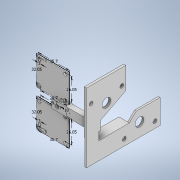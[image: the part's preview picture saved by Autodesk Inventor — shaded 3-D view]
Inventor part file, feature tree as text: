
AUTODESK INVENTOR PART (.ipt)
format: ipt  version: 2020.2 (Build 242310000, 310)  size: 299,008 bytes
history: native  units: mm
features: sketch x12, extrude x9, hole x4, projected_geometry x2
ambient origin geometry x8: Origin, YZ Plane, XZ Plane, XY Plane, X Axis, Y Axis, Z Axis, Center Point
bodies: Body1 (feature_tree)
feature tree (27):
  extrude  "Extrusion7"  Depth=6.08mm
  hole  "Hole4"  [1 undecoded]
  sketch  "Sketch16"  dims[d70=12.16mm d71=10.0mm]
  extrude  "Extrusion8"  Depth=10.0mm
  hole  "Hole5"  [1 undecoded]
  extrude  "Extrusion9"  Depth=32.05mm
  extrude  "Extrusion10"  Depth=32.05mm
  extrude  "Extrusion11"  Depth=3.0mm
  extrude  "Extrusion12"  Depth=26.05mm
  hole  "Hole6"  [1 undecoded]
  hole  "Hole7"  [1 undecoded]
  extrude  "Extrusion13"  Depth=4.0mm TaperAngle=0.0deg
  extrude  "Extrusion14"  Depth=35.0mm TaperAngle=0.0deg
  extrude  "Extrusion15"  Depth=10.0mm
  sketch  "Sketch14"  dims[d66=6.08mm d67=6.08mm]
  sketch  "Sketch15"  dims[d68=5.0mm d69=90.0deg]
  sketch  "Sketch17"  dims[d72=2.0mm d73=0.0mm]
  projected_geometry  "Projected Loop2"
  sketch  "Sketch18"  dims[d74=4.5mm d75=6.0mm d76=9.4mm d77=2.0mm d78=90.0deg d79=8.0mm d80=20.594885mm d81=10.0mm]
  projected_geometry  "Projected Loop3"
  sketch  "Sketch19"  dims[d82=35.7mm d83=32.05mm]
  sketch  "Sketch20"  dims[d84=35.7mm d85=32.05mm]
  sketch  "Sketch21"  dims[d86=3.0mm d87=3.0mm]
  sketch  "Sketch22"  dims[d88=29.7mm d89=26.05mm]
  sketch  "Sketch23"  dims[d90=3.0mm d91=3.0mm]
  sketch  "Sketch24"  dims[d92=29.7mm d93=26.05mm]
  sketch  "Sketch25"  dims[d94=1.5mm d95=0.0mm d96=3.9mm d97=6.0mm d98=8.2mm d99=2.0mm d100=90.0deg d101=8.0mm d102=20.594885mm d103=4.0mm d104=0.0mm d105=35.0mm d106=0.0mm d107=10.0mm d108=50.0mm d109=90.0deg d110=45.0mm d111=90.0deg d112=25.0mm d113=2.5mm d114=0.0mm d115=0.95mm d116=3.0mm d117=0.0mm d118=14.05mm d119=90.0deg d120=6.713mm d121=90.0deg d122=10.0mm d123=6.0mm d124=8.2mm d125=2.0mm d126=90.0deg d127=8.0mm d128=20.594885mm d129=8.0mm d130=90.0deg d131=17.5mm d132=90.0deg d133=35.0mm d134=4.2mm d135=6.0mm d136=8.2mm d137=2.0mm d138=90.0deg d139=8.0mm d140=20.594885mm d141=9.0mm d142=90.0deg d145=35.0mm d146=0.0mm d147=11.0mm d148=135.0deg d149=20.0mm d150=35.0mm d151=0.0mm d152=20.0mm d153=90.0deg d154=90.0deg d155=11.45mm d156=4.669mm d157=90.0deg d158=8.0mm d159=17.5mm d160=35.0mm d161=4.2mm d162=4.2mm d163=10.0mm d164=2.0mm d165=0.0mm d166=2.0mm d167=0.0mm d168=35.0mm d169=2.0mm d170=10.0mm d171=0.0mm d172=10.0mm]
note: 4 required parameter values undecoded (feature->parameter linkage not recoverable at this tier; creation-order binding heuristic only, values carry confidence <= 0.55)
